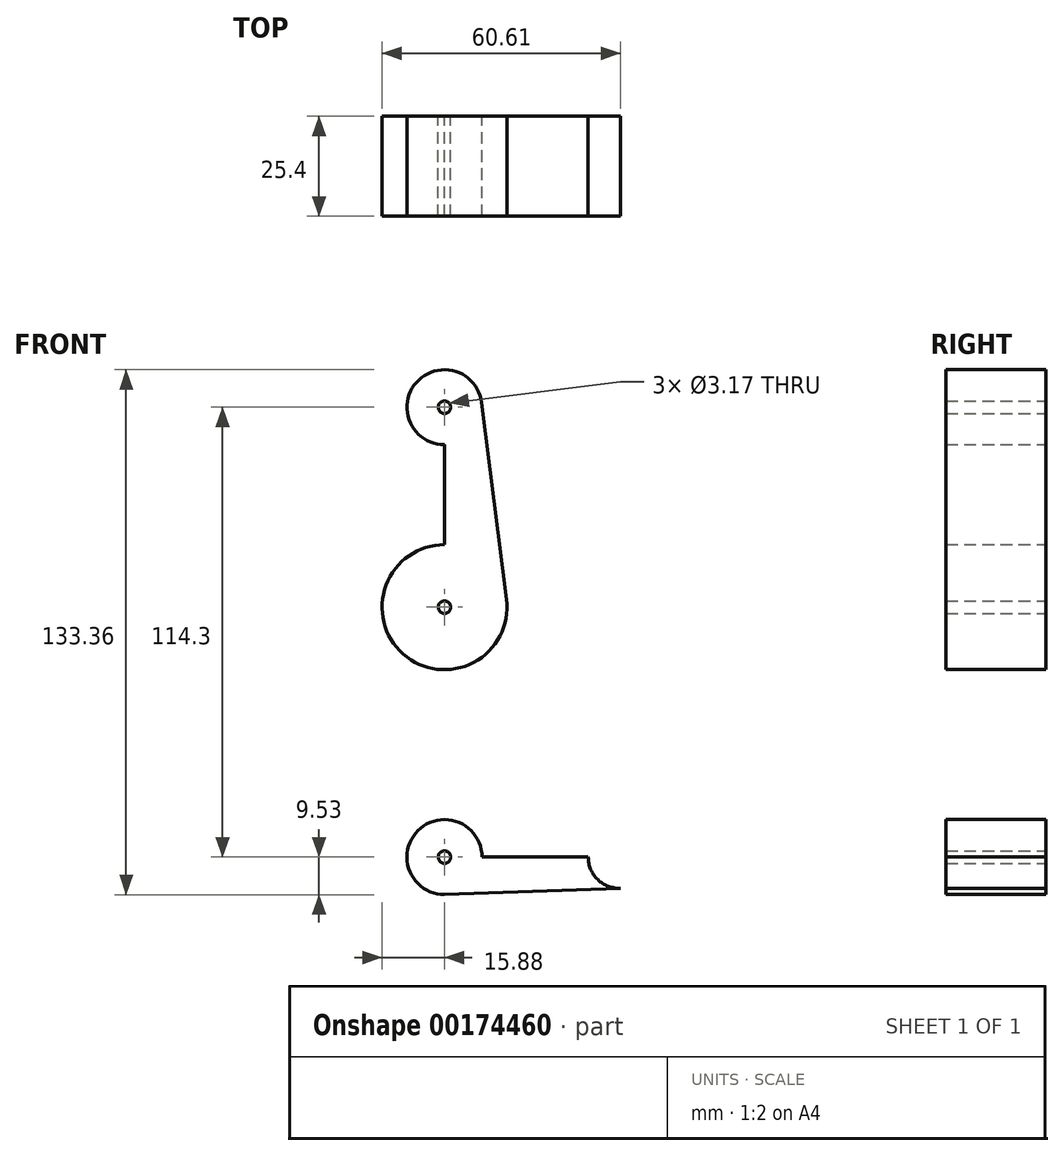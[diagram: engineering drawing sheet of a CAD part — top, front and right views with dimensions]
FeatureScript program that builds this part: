
annotation { "Feature Type Name" : "Feature", "Feature Type Description" : "" }
export const myFeature = defineFeature(function(context is Context, id is Id, definition is map)
    precondition{}
    {
        {
            var Q0;
            Q0=qCreatedBy(makeId("Front.planeOp"),FACE);
            var sketch = newSketch(context, id + "F0", { "sketchPlane" : qUnion([Q0])});
            skLineSegment(sketch, "E0", {"start": v(0, 114.3) * mm, "end": v(0, 63.5) * mm});
            skLineSegment(sketch, "E1", {"start": v(0, 63.5) * mm, "end": v(0, 0) * mm, "construction": true});
            skLineSegment(sketch, "E2", {"start": v(0, 0) * mm, "end": v(44.45, 0) * mm});
            skCircle(sketch, "E3", {"center": v(0, 114.3) * mm, "radius": 9.53 * mm});
            skCircle(sketch, "E4", {"center": v(0, 63.5) * mm, "radius": 15.88 * mm});
            skCircle(sketch, "E5", {"center": v(0, 0) * mm, "radius": 9.53 * mm});
            skCircle(sketch, "E6", {"center": v(44.45, 0) * mm, "radius": 7.94 * mm});
            skLineSegment(sketch, "E7", {"start": v(-9.45, 115.5) * mm, "end": v(-15.75, 65.48) * mm});
            skLineSegment(sketch, "E8", {"start": v(9.45, 115.5) * mm, "end": v(15.75, 65.48) * mm});
            skLineSegment(sketch, "E9", {"start": v(-15.75, 61.52) * mm, "end": v(-9.57, 0) * mm});
            skLineSegment(sketch, "E10", {"start": v(15.75, 61.52) * mm, "end": v(11.13, 15.9) * mm});
            skLineSegment(sketch, "E11", {"start": v(17.23, 8.91) * mm, "end": v(44.73, 7.93) * mm});
            skLineSegment(sketch, "E12", {"start": v(0, -9.53) * mm, "end": v(44.73, -7.93) * mm});
            skCircle(sketch, "E13", {"center": v(0, 114.3) * mm, "radius": 1.59 * mm});
            skCircle(sketch, "E14", {"center": v(0, 63.5) * mm, "radius": 1.59 * mm});
            skCircle(sketch, "E15", {"center": v(0, 0) * mm, "radius": 1.59 * mm});
            skCircle(sketch, "E16", {"center": v(44.45, 0) * mm, "radius": 1.59 * mm});
            skCircle(sketch, "E17", {"center": v(-5.84, 100.03) * mm, "radius": 1.59 * mm});
            skArc(sketch, "E18.filletArc", {"start": v(11.13, 15.9) * mm, "mid": v(12.67, 11.08) * mm, "end": v(17.23, 8.91) * mm});
            skSolve(sketch);
        }
        {
            var Q0;
            Q0=makeQuery(id+"F0.imprint","IMPRINT",FACE,{"disambiguationData":[TD([[makeQuery(id+"F0.imprint","IMPRINT",EDGE,{"derivedFrom":sQuery(id+"F0.wireOp",EDGE,"E13")}),-1.0]])]});
            var Q1;
            {var subQ5=sQuery(id+"F0.wireOp",EDGE,"E8");Q1=makeQuery(id+"F0.imprint","IMPRINT",FACE,{"disambiguationData":[TD([[makeQuery(id+"F0.imprint","IMPRINT",EDGE,{"derivedFrom":subQ5}),-1.0]])]});}
            var Q2;
            Q2=makeQuery(id+"F0.imprint","IMPRINT",FACE,{"disambiguationData":[TD([[makeQuery(id+"F0.imprint","IMPRINT",EDGE,{"derivedFrom":sQuery(id+"F0.wireOp",EDGE,"E14")}),-1.0]])]});
            var Q3;
            {var subQ0=sQuery(id+"F0.wireOp",EDGE,"E5");var subQ1=sQuery(id+"F0.wireOp",EDGE,"E2");var subQ2=makeQuery(id+"F0.imprint","INTERSECT",VERTEX,{"derivedFrom":[subQ1,subQ0]});Q3=makeQuery(id+"F0.imprint","IMPRINT",FACE,{"disambiguationData":[TD([[makeQuery(id+"F0.imprint","IMPRINT",EDGE,{"disambiguationData":[TD([[subQ2,-1.0]])],"derivedFrom":subQ1}),-1.0]])]});}
            var Q4;
            Q4=makeQuery(id+"F0.imprint","IMPRINT",FACE,{"disambiguationData":[TD([[makeQuery(id+"F0.imprint","IMPRINT",EDGE,{"derivedFrom":sQuery(id+"F0.wireOp",EDGE,"E15")}),-1.0]])]});
            extrude(context, id + "F1", {"entities" : qUnion([Q0, Q1, Q2, Q3, Q4]), "depth" : 25.4 * mm});
        }
    });
